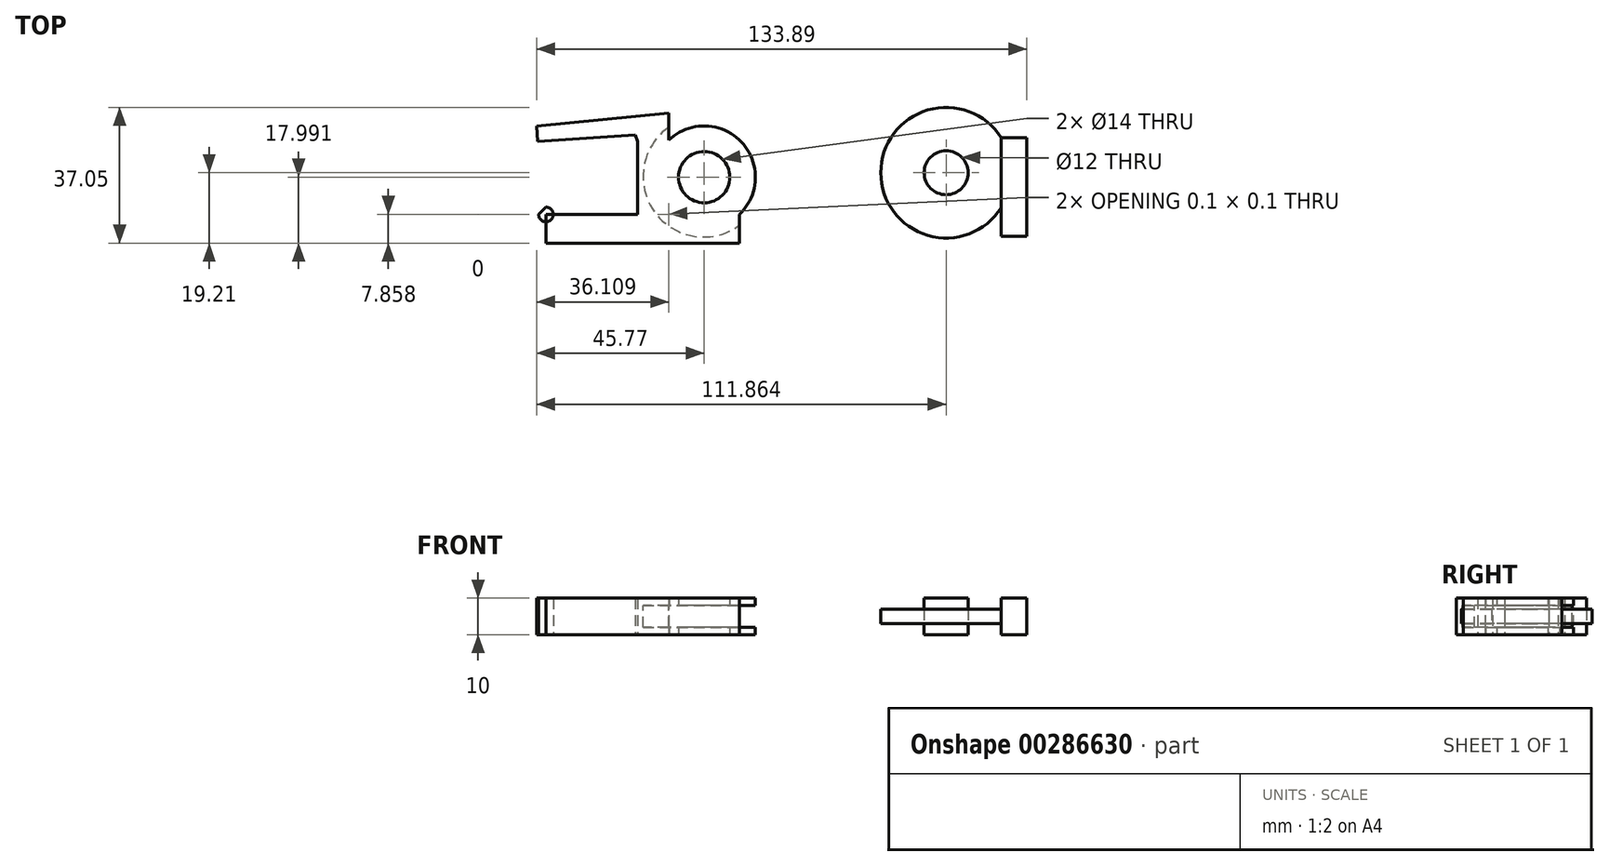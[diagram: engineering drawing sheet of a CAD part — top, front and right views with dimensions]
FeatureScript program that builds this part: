
annotation { "Feature Type Name" : "Feature", "Feature Type Description" : "" }
export const myFeature = defineFeature(function(context is Context, id is Id, definition is map)
    precondition{}
    {
        {
            var Q0;
            Q0=qCreatedBy(makeId("Top.planeOp"),FACE);
            var sketch = newSketch(context, id + "F0", { "sketchPlane" : qUnion([Q0])});
            skLineSegment(sketch, "E0", {"start": v(45.62, 33.15) * mm, "end": v(45.62, 13.93) * mm});
            skArc(sketch, "E1", {"start": v(45.62, 33.15) * mm, "mid": v(12.76, 23.54) * mm, "end": v(45.62, 13.93) * mm});
            skCircle(sketch, "E2", {"center": v(30.6, 23.54) * mm, "radius": 6 * mm});
            skLineSegment(sketch, "E3", {"start": v(45.62, 13.93) * mm, "end": v(45.62, 6.15) * mm});
            skLineSegment(sketch, "E4", {"start": v(45.62, 6.15) * mm, "end": v(52.62, 6.15) * mm});
            skLineSegment(sketch, "E5", {"start": v(45.62, 33.15) * mm, "end": v(52.62, 33.15) * mm});
            skLineSegment(sketch, "E6", {"start": v(52.62, 33.15) * mm, "end": v(52.62, 6.15) * mm});
            skLineSegment(sketch, "E7", {"start": v(-25.9, 12.14) * mm, "end": v(-45.1, 12.14) * mm});
            skArc(sketch, "E8", {"start": v(-25.9, 12.14) * mm, "mid": v(-35.5, 36.32) * mm, "end": v(-45.1, 12.14) * mm});
            skCircle(sketch, "E9", {"center": v(-35.5, 22.32) * mm, "radius": 7 * mm});
            skLineSegment(sketch, "E10", {"start": v(-45.1, 12.14) * mm, "end": v(-53.7, 12.14) * mm});
            skLineSegment(sketch, "E11", {"start": v(-53.7, 12.14) * mm, "end": v(-53.7, 4.33) * mm});
            skLineSegment(sketch, "E12", {"start": v(-25.9, 12.14) * mm, "end": v(-25.9, 4.33) * mm});
            skLineSegment(sketch, "E13", {"start": v(-25.9, 4.33) * mm, "end": v(-53.7, 4.33) * mm});
            skLineSegment(sketch, "E14", {"start": v(-45.21, 12.12) * mm, "end": v(-45.21, 32.4) * mm});
            skLineSegment(sketch, "E15", {"start": v(-53.7, 12.14) * mm, "end": v(-53.7, 32.14) * mm});
            skLineSegment(sketch, "E16", {"start": v(-53.7, 32.14) * mm, "end": v(-45.21, 32.4) * mm});
            skLineSegment(sketch, "E17", {"start": v(-53.7, 12.14) * mm, "end": v(-78.7, 12.14) * mm});
            skLineSegment(sketch, "E18", {"start": v(-53.7, 4.33) * mm, "end": v(-78.7, 4.33) * mm});
            skLineSegment(sketch, "E19", {"start": v(-78.7, 4.33) * mm, "end": v(-78.7, 12.14) * mm});
            skArc(sketch, "E20", {"start": v(-78.7, 14.14) * mm, "mid": v(-77.3, 10.72) * mm, "end": v(-80.7, 12.14) * mm});
            skLineSegment(sketch, "E21", {"start": v(-78.7, 14.14) * mm, "end": v(-78.7, 12.14) * mm});
            skLineSegment(sketch, "E22", {"start": v(-78.7, 14.14) * mm, "end": v(-80.7, 12.14) * mm});
            skLineSegment(sketch, "E23", {"start": v(-53.7, 32.14) * mm, "end": v(-54.3, 33.86) * mm});
            skLineSegment(sketch, "E24", {"start": v(-54.3, 33.86) * mm, "end": v(-81, 32.14) * mm});
            skLineSegment(sketch, "E25", {"start": v(-81, 32.14) * mm, "end": v(-81.27, 36.21) * mm});
            skLineSegment(sketch, "E26", {"start": v(-81.27, 36.21) * mm, "end": v(-45.21, 39.86) * mm});
            skLineSegment(sketch, "E27", {"start": v(-45.21, 39.86) * mm, "end": v(-45.21, 32.4) * mm});
            skSolve(sketch);
        }
        {
            var Q0;
            Q0=makeQuery(id+"F0.imprint","IMPRINT",FACE,{"disambiguationData":[TD([[makeQuery(id+"F0.imprint","IMPRINT",EDGE,{"derivedFrom":sQuery(id+"F0.wireOp",EDGE,"E0")}),1.0]])]});
            var Q1;
            Q1=makeQuery(id+"F0.imprint","IMPRINT",FACE,{"disambiguationData":[TD([[makeQuery(id+"F0.imprint","IMPRINT",EDGE,{"derivedFrom":sQuery(id+"F0.wireOp",EDGE,"E2")}),1.0]])]});
            extrude(context, id + "F1", {"entities" : qUnion([Q0, Q1]), "depth" : 5 * mm, "hasSecondDirection" : true, "secondDirectionOppositeDirection" : true, "secondDirectionDepth" : 5 * mm});
        }
        {
            var Q0;
            Q0=makeQuery(id+"F0.imprint","IMPRINT",FACE,{"disambiguationData":[TD([[makeQuery(id+"F0.imprint","IMPRINT",EDGE,{"derivedFrom":sQuery(id+"F0.wireOp",EDGE,"E0")}),-1.0]])]});
            extrude(context, id + "F2", {"entities" : qUnion([Q0]), "depth" : 2 * mm, "hasSecondDirection" : true, "secondDirectionOppositeDirection" : true, "secondDirectionDepth" : 2 * mm});
        }
        {
            var Q0;
            {var subQ0=sQuery(id+"F0.wireOp",EDGE,"E21");Q0=makeQuery(id+"F0.imprint","IMPRINT",FACE,{"disambiguationData":[TD([[makeQuery(id+"F0.imprint","IMPRINT",EDGE,{"derivedFrom":subQ0}),-1.0]])]});}
            var Q1;
            {var subQ0=sQuery(id+"F0.wireOp",EDGE,"E21");Q1=makeQuery(id+"F0.imprint","IMPRINT",FACE,{"disambiguationData":[TD([[makeQuery(id+"F0.imprint","IMPRINT",EDGE,{"derivedFrom":subQ0}),1.0]])]});}
            var Q2;
            {var subQ1=sQuery(id+"F0.wireOp",EDGE,"E17");var subQ3=sQuery(id+"F0.wireOp",EDGE,"E20");var subQ4=makeQuery(id+"F0.imprint","INTERSECT",VERTEX,{"derivedFrom":[subQ1,subQ3]});Q2=makeQuery(id+"F0.imprint","IMPRINT",FACE,{"disambiguationData":[TD([[makeQuery(id+"F0.imprint","IMPRINT",EDGE,{"disambiguationData":[TD([[subQ4,-1.0]])],"derivedFrom":subQ3}),-1.0]])]});}
            var Q3;
            {var subQ2=sQuery(id+"F0.wireOp",EDGE,"E11");Q3=makeQuery(id+"F0.imprint","IMPRINT",FACE,{"disambiguationData":[TD([[makeQuery(id+"F0.imprint","IMPRINT",EDGE,{"derivedFrom":subQ2}),-1.0]])]});}
            var Q4;
            {var subQ3=sQuery(id+"F0.wireOp",EDGE,"E7");Q4=makeQuery(id+"F0.imprint","IMPRINT",FACE,{"disambiguationData":[TD([[makeQuery(id+"F0.imprint","IMPRINT",EDGE,{"derivedFrom":subQ3}),1.0]])]});}
            var Q5;
            {var subQ5=sQuery(id+"F0.wireOp",EDGE,"E15");Q5=makeQuery(id+"F0.imprint","IMPRINT",FACE,{"disambiguationData":[TD([[makeQuery(id+"F0.imprint","IMPRINT",EDGE,{"derivedFrom":subQ5}),-1.0]])]});}
            var Q6;
            Q6=makeQuery(id+"F0.imprint","IMPRINT",FACE,{"disambiguationData":[TD([[makeQuery(id+"F0.imprint","IMPRINT",EDGE,{"derivedFrom":sQuery(id+"F0.wireOp",EDGE,"E16")}),1.0]])]});
            extrude(context, id + "F3", {"entities" : qUnion([Q0, Q1, Q2, Q3, Q4, Q5, Q6]), "depth" : 5 * mm, "hasSecondDirection" : true, "secondDirectionOppositeDirection" : true, "secondDirectionDepth" : 5 * mm});
        }
        {
            var Q0;
            {var subQ0=sQuery(id+"F0.wireOp",EDGE,"E14");var subQ1=sQuery(id+"F0.wireOp",EDGE,"E8");var subQ3=makeQuery(id+"F0.imprint","INTERSECT",VERTEX,{"derivedFrom":[subQ1,subQ0]});Q0=makeQuery(id+"F0.imprint","IMPRINT",FACE,{"disambiguationData":[TD([[makeQuery(id+"F0.imprint","IMPRINT",EDGE,{"disambiguationData":[TD([[subQ3,1.0]])],"derivedFrom":subQ1}),1.0]])]});}
            var Q1;
            {var subQ1=sQuery(id+"F0.wireOp",EDGE,"E7");Q1=makeQuery(id+"F0.imprint","IMPRINT",FACE,{"disambiguationData":[TD([[makeQuery(id+"F0.imprint","IMPRINT",EDGE,{"derivedFrom":subQ1}),-1.0]])]});}
            extrude(context, id + "F4", {"entities" : qUnion([Q0, Q1]), "operationType" : NewBodyOperationType.ADD, "depth" : 5 * mm, "hasSecondDirection" : true, "secondDirectionOppositeDirection" : true, "secondDirectionDepth" : 5 * mm});
        }
        {
            var Q0;
            {var subQ0=sQuery(id+"F0.wireOp",EDGE,"E8");var subQ1=sQuery(id+"F0.wireOp",EDGE,"E7");Q0=makeQuery(id+"F4.boolean.opBoolean","MERGE",FACE,{"derivedFrom":[makeQuery(id+"F3.opExtrude","CAP_FACE",FACE,{"disambiguationData":[OSD([subQ1,subQ0,sQuery(id+"F0.wireOp",EDGE,"E10"),sQuery(id+"F0.wireOp",EDGE,"E12"),sQuery(id+"F0.wireOp",EDGE,"E13"),sQuery(id+"F0.wireOp",EDGE,"E14"),sQuery(id+"F0.wireOp",EDGE,"E15"),sQuery(id+"F0.wireOp",EDGE,"E17"),sQuery(id+"F0.wireOp",EDGE,"E18"),sQuery(id+"F0.wireOp",EDGE,"E19"),sQuery(id+"F0.wireOp",EDGE,"E20"),sQuery(id+"F0.wireOp",EDGE,"E22"),sQuery(id+"F0.wireOp",EDGE,"E23"),sQuery(id+"F0.wireOp",EDGE,"E24"),sQuery(id+"F0.wireOp",EDGE,"E25"),sQuery(id+"F0.wireOp",EDGE,"E26"),sQuery(id+"F0.wireOp",EDGE,"E27")])],"isStart":false}),makeQuery(id+"F4.opExtrude","CAP_FACE",FACE,{"disambiguationData":[OSD([subQ1,subQ0,sQuery(id+"F0.wireOp",EDGE,"E9")])],"isStart":false})]});}
            var sketch = newSketch(context, id + "F5", { "sketchPlane" : qUnion([Q0])});
            skSolve(sketch);
        }
        {
            var Q0;
            Q0=qCreatedBy(makeId("Top.planeOp"),FACE);
            var sketch = newSketch(context, id + "F6", { "sketchPlane" : qUnion([Q0])});
            skCircle(sketch, "E28", {"center": v(-35.67, 22.48) * mm, "radius": 16.5 * mm});
            skSolve(sketch);
        }
        {
            var Q0;
            Q0=makeQuery(id+"F6.imprint","IMPRINT",FACE,{"disambiguationData":[TD([[makeQuery(id+"F6.imprint","IMPRINT",EDGE,{"derivedFrom":sQuery(id+"F6.wireOp",EDGE,"E28")}),1.0]])]});
            extrude(context, id + "F7", {"entities" : qUnion([Q0]), "operationType" : NewBodyOperationType.REMOVE, "oppositeDirection" : true, "depth" : 3 * mm, "hasSecondDirection" : true, "secondDirectionOppositeDirection" : false, "secondDirectionDepth" : 3 * mm});
        }
    });
